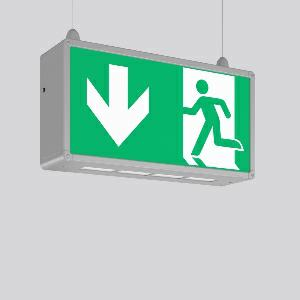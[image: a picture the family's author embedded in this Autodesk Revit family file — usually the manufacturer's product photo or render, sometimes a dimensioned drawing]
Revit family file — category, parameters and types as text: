
# Revit family: rechteck_seilpendel_671351_004_04_37dd
name_source: partatom
category: Lighting Fixtures
units: mm (PartAtom-declared; Revit-internal decimal feet)

## family parameters
Cut with Voids When Loaded = No
Host = Face
Light Source = No
Part Type = Normal
Room Calculation Point = No
Round Connector Dimension = Use Diameter
Shared = No

## types (1)
- RECHTECK seilpendel
    Apparent Load = 0 VA
    Default Elevation = 1800 mm
    Description = Series: RECHTECK
Rectangular pendant luminaire in classic design. For escape route identification. Housing: aluminium, with plastic corner connectors. Display panels: plastic, opal, with motifs on one side/on both sides. Pendant luminaires (suspension provided on site) ready for connection to two suspension cables or chains. Driver integrated. Self-contained system with automatic self-test and feedback to the RZB monitoring system MULTIDIGIT. Please indicate legend number when placing your order! 
Colour: anodised aluminium
Length: 485 mm
Width: 125 mm
Height: 250 mm
Weight: 3.11 kg
Operating mode: maintained power mode
Viewing Distance: 43 m
Duration time: 3 h
Lamp: LED
Socket: without socket
Colour temperature: 6500K
Colour rendering index (CRI): 70
System power: 9.1 W
Control gear: Regulated power supply
Protection class: I
Type of protection: IP 44
    Height = 250 mm
    Lamp = 0 x
    Length = 485 mm
    Luminous efficacy = 0 lm/W
    Manufacturer = RZB
    ModVariant = No
    Model = 671351.004.04
    Mounting Place = Ceiling
    Mounting Type = Pendant
    Number of Poles = 1
    OnlyDefault = Yes
    Power Factor = 1
    Product Name = RECHTECK seilpendel
    Product group = Pendant luminaires
    ProductGroupID = 902
    Protection Class = Protection class I
    Protection Degree = IP 44
    RLX_Detail_Level = 1
    RLX_Emergency_Light_Flux = 0 lm
    RLX_Emergency_Type = 0
    RLX_Emergency_Type_DB = No
    RlxData = <blob elided: 57293 chars, md5=5133ff46>
    Standby Power = 0 W
    System Light Flux = 0 lm
    System Power = 0 W
    Type Comments = Product without accessories
    Type Image = 671351.004.jpg
    URL = http://relux.com
    VarID = ---
    Voltage = 230 V
    Voltage Range = 220-240 V
    Weight = 0.00 kg
    Width = 125 mm

## geometry (parser evidence)
native form markers: Blend x4, Sweep x9
no freeform markers — native parametric forms only
